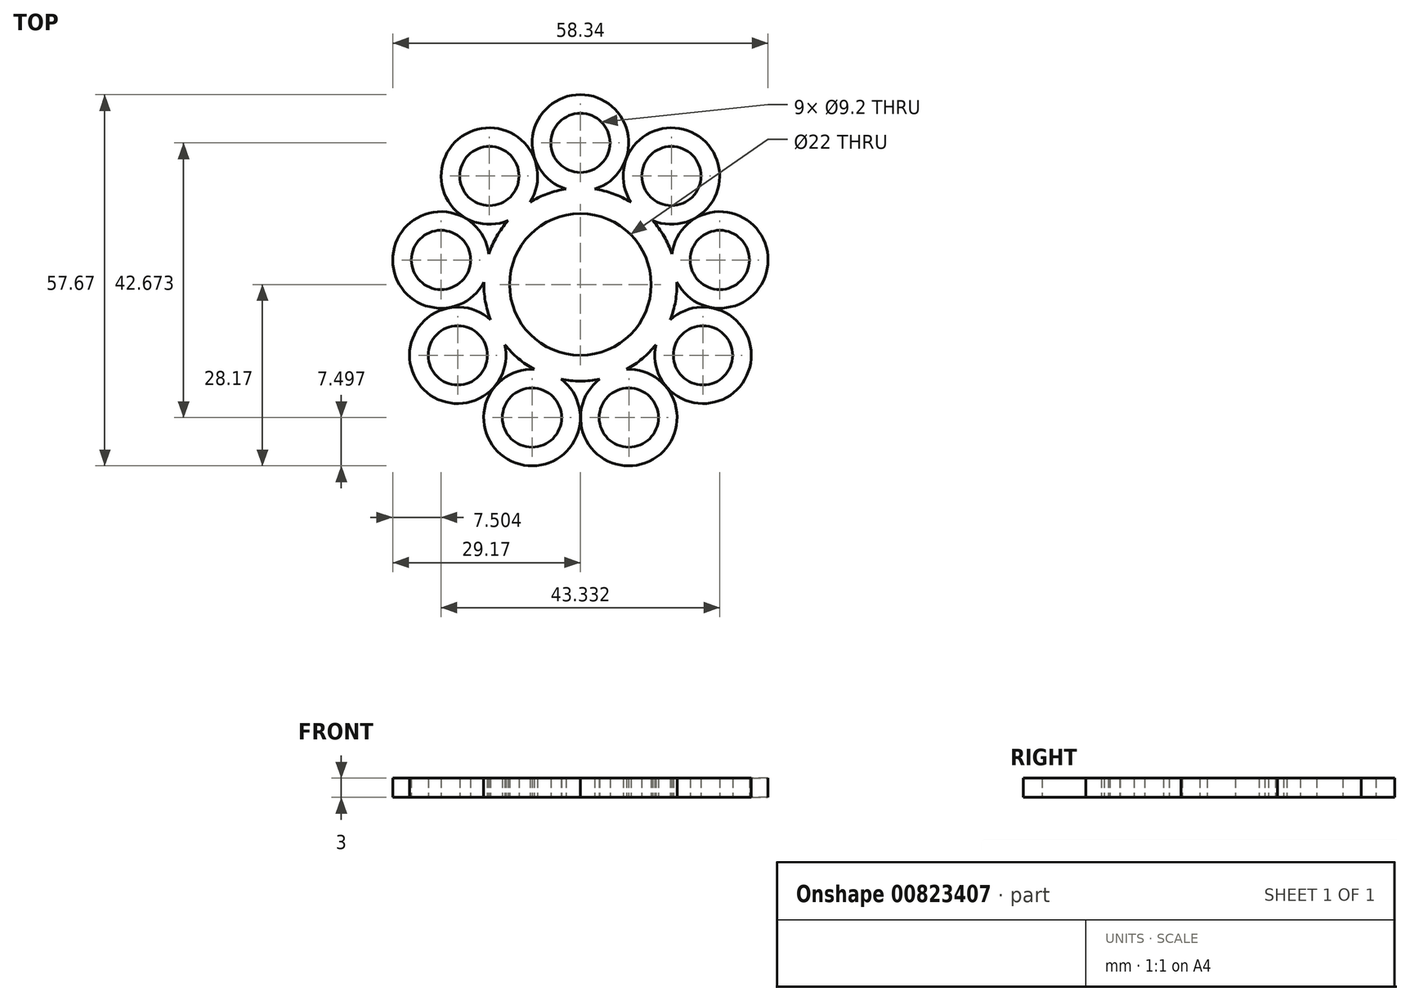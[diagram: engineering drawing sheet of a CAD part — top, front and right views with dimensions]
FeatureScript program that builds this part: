
annotation { "Feature Type Name" : "Feature", "Feature Type Description" : "" }
export const myFeature = defineFeature(function(context is Context, id is Id, definition is map)
    precondition{}
    {
        {
            var Q0;
            Q0=qCreatedBy(makeId("Top.planeOp"),FACE);
            var sketch = newSketch(context, id + "F0", { "sketchPlane" : qUnion([Q0])});
            skArc(sketch, "E0", {"start": v(5.5, 9.53) * mm, "mid": v(0, 11) * mm, "end": v(-5.5, 9.53) * mm});
            skArc(sketch, "E1", {"start": v(-2.22, 14.84) * mm, "mid": v(-4.95, 14.16) * mm, "end": v(-7.5, 13) * mm});
            skLineSegment(sketch, "E2", {"start": v(0, 0) * mm, "end": v(0, 22) * mm});
            skCircle(sketch, "E3", {"center": v(0, 22) * mm, "radius": 4.6 * mm});
            skArc(sketch, "E4", {"start": v(2.22, 14.84) * mm, "mid": v(0, 29.5) * mm, "end": v(-2.22, 14.84) * mm});
            skArc(sketch, "E5.trimOffspring", {"start": v(7.5, 13) * mm, "mid": v(4.95, 14.16) * mm, "end": v(2.22, 14.84) * mm});
            skArc(sketch, "E6.1.0", {"start": v(-7.84, 12.79) * mm, "mid": v(-18.96, 22.6) * mm, "end": v(-11.23, 9.94) * mm});
            skArc(sketch, "E6.1.1", {"start": v(-11.23, 9.94) * mm, "mid": v(-12.9, 7.67) * mm, "end": v(-14.1, 5.13) * mm});
            skArc(sketch, "E6.1.2", {"start": v(-2.6, 14.77) * mm, "mid": v(-5.31, 14.03) * mm, "end": v(-7.84, 12.79) * mm});
            skArc(sketch, "E6.1.3", {"start": v(-1.91, 10.83) * mm, "mid": v(-7.07, 8.43) * mm, "end": v(-10.34, 3.76) * mm});
            skCircle(sketch, "E6.1.4", {"center": v(-14.14, 16.85) * mm, "radius": 4.6 * mm});
            skArc(sketch, "E6.2.0", {"start": v(-14.22, 4.76) * mm, "mid": v(-29.05, 5.12) * mm, "end": v(-15, 0.4) * mm});
            skArc(sketch, "E6.2.1", {"start": v(-15, 0.4) * mm, "mid": v(-14.8, -2.41) * mm, "end": v(-14.1, -5.13) * mm});
            skArc(sketch, "E6.2.2", {"start": v(-11.5, 9.64) * mm, "mid": v(-13.09, 7.33) * mm, "end": v(-14.22, 4.76) * mm});
            skArc(sketch, "E6.2.3", {"start": v(-8.43, 7.07) * mm, "mid": v(-10.83, 1.91) * mm, "end": v(-10.34, -3.76) * mm});
            skCircle(sketch, "E6.2.4", {"center": v(-21.67, 3.82) * mm, "radius": 4.6 * mm});
            skArc(sketch, "E6.3.0", {"start": v(-13.96, -5.5) * mm, "mid": v(-25.55, -14.75) * mm, "end": v(-11.74, -9.34) * mm});
            skArc(sketch, "E6.3.1", {"start": v(-11.74, -9.34) * mm, "mid": v(-9.8, -11.36) * mm, "end": v(-7.5, -13) * mm});
            skArc(sketch, "E6.3.2", {"start": v(-15, 0) * mm, "mid": v(-14.74, -2.8) * mm, "end": v(-13.96, -5.5) * mm});
            skArc(sketch, "E6.3.3", {"start": v(-11, 0) * mm, "mid": v(-9.53, -5.5) * mm, "end": v(-5.5, -9.53) * mm});
            skCircle(sketch, "E6.3.4", {"center": v(-19.05, -11) * mm, "radius": 4.6 * mm});
            skArc(sketch, "E6.4.0", {"start": v(-7.16, -13.18) * mm, "mid": v(-10.09, -27.72) * mm, "end": v(-3, -14.7) * mm});
            skArc(sketch, "E6.4.1", {"start": v(-3, -14.7) * mm, "mid": v(-0.2, -15) * mm, "end": v(2.6, -14.77) * mm});
            skArc(sketch, "E6.4.2", {"start": v(-11.5, -9.64) * mm, "mid": v(-9.5, -11.62) * mm, "end": v(-7.16, -13.18) * mm});
            skArc(sketch, "E6.4.3", {"start": v(-8.43, -7.07) * mm, "mid": v(-3.76, -10.34) * mm, "end": v(1.91, -10.83) * mm});
            skCircle(sketch, "E6.4.4", {"center": v(-7.52, -20.67) * mm, "radius": 4.6 * mm});
            skArc(sketch, "E6.5.0", {"start": v(3, -14.7) * mm, "mid": v(10.09, -27.72) * mm, "end": v(7.16, -13.18) * mm});
            skArc(sketch, "E6.5.1", {"start": v(7.16, -13.18) * mm, "mid": v(9.5, -11.62) * mm, "end": v(11.5, -9.64) * mm});
            skArc(sketch, "E6.5.2", {"start": v(-2.6, -14.77) * mm, "mid": v(0.2, -15) * mm, "end": v(3, -14.7) * mm});
            skArc(sketch, "E6.5.3", {"start": v(-1.91, -10.83) * mm, "mid": v(3.76, -10.34) * mm, "end": v(8.43, -7.07) * mm});
            skCircle(sketch, "E6.5.4", {"center": v(7.52, -20.67) * mm, "radius": 4.6 * mm});
            skArc(sketch, "E6.6.0", {"start": v(11.74, -9.34) * mm, "mid": v(25.55, -14.75) * mm, "end": v(13.96, -5.5) * mm});
            skArc(sketch, "E6.6.1", {"start": v(13.96, -5.5) * mm, "mid": v(14.74, -2.8) * mm, "end": v(15, 0) * mm});
            skArc(sketch, "E6.6.2", {"start": v(7.5, -13) * mm, "mid": v(9.8, -11.36) * mm, "end": v(11.74, -9.34) * mm});
            skArc(sketch, "E6.6.3", {"start": v(5.5, -9.53) * mm, "mid": v(9.53, -5.5) * mm, "end": v(11, 0) * mm});
            skCircle(sketch, "E6.6.4", {"center": v(19.05, -11) * mm, "radius": 4.6 * mm});
            skArc(sketch, "E6.7.0", {"start": v(15, 0.4) * mm, "mid": v(29.05, 5.12) * mm, "end": v(14.22, 4.76) * mm});
            skArc(sketch, "E6.7.1", {"start": v(14.22, 4.76) * mm, "mid": v(13.09, 7.33) * mm, "end": v(11.5, 9.64) * mm});
            skArc(sketch, "E6.7.2", {"start": v(14.1, -5.13) * mm, "mid": v(14.8, -2.41) * mm, "end": v(15, 0.4) * mm});
            skArc(sketch, "E6.7.3", {"start": v(10.34, -3.76) * mm, "mid": v(10.83, 1.91) * mm, "end": v(8.43, 7.07) * mm});
            skCircle(sketch, "E6.7.4", {"center": v(21.67, 3.82) * mm, "radius": 4.6 * mm});
            skArc(sketch, "E6.8.0", {"start": v(11.23, 9.94) * mm, "mid": v(18.96, 22.6) * mm, "end": v(7.84, 12.79) * mm});
            skArc(sketch, "E6.8.1", {"start": v(7.84, 12.79) * mm, "mid": v(5.31, 14.03) * mm, "end": v(2.6, 14.77) * mm});
            skArc(sketch, "E6.8.2", {"start": v(14.1, 5.13) * mm, "mid": v(12.9, 7.67) * mm, "end": v(11.23, 9.94) * mm});
            skArc(sketch, "E6.8.3", {"start": v(10.34, 3.76) * mm, "mid": v(7.07, 8.43) * mm, "end": v(1.91, 10.83) * mm});
            skCircle(sketch, "E6.8.4", {"center": v(14.14, 16.85) * mm, "radius": 4.6 * mm});
            skSolve(sketch);
        }
        {
            var Q0;
            Q0 = qSketchRegion(id + "F0", true);
            extrude(context, id + "F1", {"entities" : qUnion([Q0]), "depth" : 3 * mm, "offsetDistance" : 25 * mm});
        }
    });
